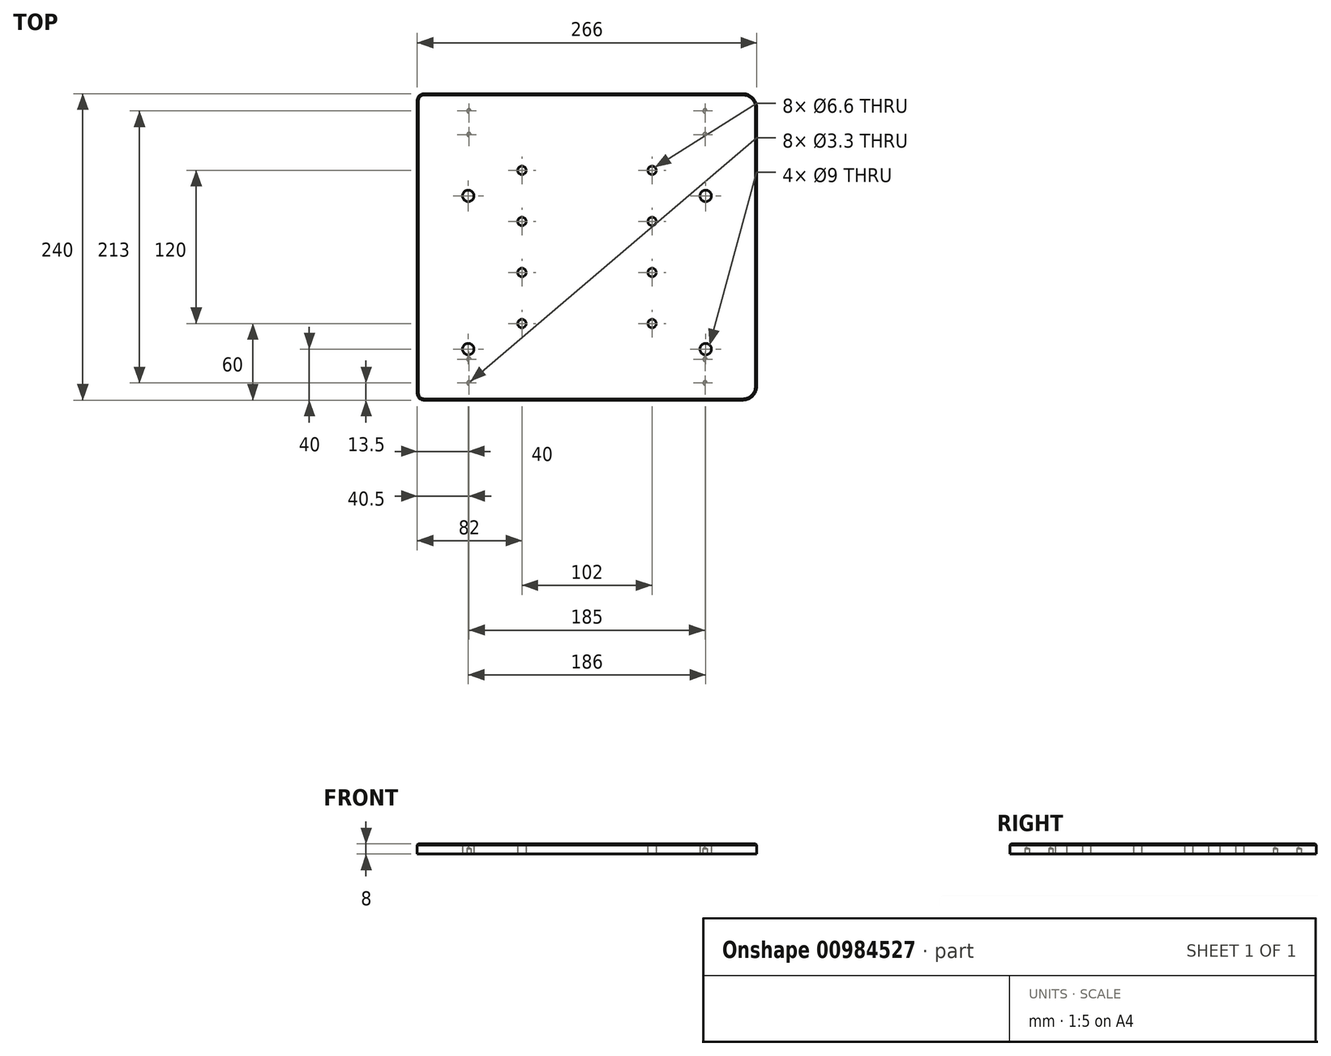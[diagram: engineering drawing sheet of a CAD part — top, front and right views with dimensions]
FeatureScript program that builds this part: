
annotation { "Feature Type Name" : "Feature", "Feature Type Description" : "" }
export const myFeature = defineFeature(function(context is Context, id is Id, definition is map)
    precondition{}
    {
        {
            var Q0;
            Q0=qCreatedBy(makeId("Top.planeOp"),FACE);
            var sketch = newSketch(context, id + "F0", { "sketchPlane" : qUnion([Q0])});
            skLineSegment(sketch, "E0.bottom", {"start": v(122.23, -120) * mm, "end": v(-127.75, -120) * mm});
            skLineSegment(sketch, "E0.top", {"start": v(122.23, 120) * mm, "end": v(-127.75, 120) * mm});
            skLineSegment(sketch, "E0.left", {"start": v(133, -109.23) * mm, "end": v(133, 109.23) * mm});
            skLineSegment(sketch, "E0.right", {"start": v(-133, -114.75) * mm, "end": v(-133, 114.75) * mm});
            skPoint(sketch, "E0.middle", {"position": v(0, 0) * mm});
            skPoint(sketch, "E1.visualSharp", {"position": v(133, 120) * mm});
            skArc(sketch, "E1.filletArc", {"start": v(133, 109.23) * mm, "mid": v(129.85, 116.85) * mm, "end": v(122.23, 120) * mm});
            skPoint(sketch, "E2.visualSharp", {"position": v(133, -120) * mm});
            skArc(sketch, "E2.filletArc", {"start": v(122.23, -120) * mm, "mid": v(129.85, -116.85) * mm, "end": v(133, -109.23) * mm});
            skPoint(sketch, "E3.visualSharp", {"position": v(-133, -120) * mm});
            skArc(sketch, "E3.filletArc", {"start": v(-133, -114.75) * mm, "mid": v(-131.46, -118.46) * mm, "end": v(-127.75, -120) * mm});
            skPoint(sketch, "E4.visualSharp", {"position": v(-133, 120) * mm});
            skArc(sketch, "E4.filletArc", {"start": v(-127.75, 120) * mm, "mid": v(-131.46, 118.46) * mm, "end": v(-133, 114.75) * mm});
            skPoint(sketch, "E5", {"position": v(-93, -80) * mm});
            skPoint(sketch, "E6", {"position": v(-93, 40) * mm});
            skPoint(sketch, "E7", {"position": v(93, 40) * mm});
            skPoint(sketch, "E8", {"position": v(93, -80) * mm});
            skPoint(sketch, "E9", {"position": v(-51, -60) * mm});
            skPoint(sketch, "E10", {"position": v(-51, -20) * mm});
            skPoint(sketch, "E11", {"position": v(-51, 20) * mm});
            skPoint(sketch, "E12", {"position": v(-51, 60) * mm});
            skPoint(sketch, "E13", {"position": v(51, 60) * mm});
            skPoint(sketch, "E14", {"position": v(51, 20) * mm});
            skPoint(sketch, "E15", {"position": v(51, -60) * mm});
            skPoint(sketch, "E16", {"position": v(51, -20) * mm});
            skPoint(sketch, "E17", {"position": v(-92.5, -106.5) * mm});
            skPoint(sketch, "E18", {"position": v(-92.5, -88) * mm});
            skPoint(sketch, "E19", {"position": v(-92.5, 106.5) * mm});
            skPoint(sketch, "E20", {"position": v(-92.5, 88) * mm});
            skPoint(sketch, "E21.MirrorP", {"position": v(92.5, -106.5) * mm});
            skPoint(sketch, "E22.MirrorP", {"position": v(92.5, -88) * mm});
            skPoint(sketch, "E23.MirrorP", {"position": v(92.5, 88) * mm});
            skPoint(sketch, "E24.MirrorP", {"position": v(92.5, 106.5) * mm});
            skSolve(sketch);
        }
        {
            var Q0;
            Q0=makeQuery(id+"F0.imprint","IMPRINT",FACE,{"disambiguationData":[TD([[makeQuery(id+"F0.imprint","IMPRINT",EDGE,{"derivedFrom":sQuery(id+"F0.wireOp",EDGE,"E0.bottom")}),-1.0]])]});
            extrude(context, id + "F1", {"entities" : qUnion([Q0]), "depth" : 8 * mm, "offsetDistance" : 25 * mm});
        }
        {
            var Q0;
            Q0=makeQuery(id+"F1.opExtrude","CAP_FACE",FACE,{"disambiguationData":[OSD([sQuery(id+"F0.wireOp",EDGE,"E0.bottom"),sQuery(id+"F0.wireOp",EDGE,"E0.top"),sQuery(id+"F0.wireOp",EDGE,"E0.left"),sQuery(id+"F0.wireOp",EDGE,"E0.right"),sQuery(id+"F0.wireOp",EDGE,"E1.filletArc"),sQuery(id+"F0.wireOp",EDGE,"E2.filletArc"),sQuery(id+"F0.wireOp",EDGE,"E3.filletArc"),sQuery(id+"F0.wireOp",EDGE,"E4.filletArc")])],"isStart":false});
            chamfer(context, id + "F2", {"entities" : qUnion([Q0]), "width" : 1 * mm, "tangentPropagation" : true});
        }
        {
            var Q0;
            Q0=sQuery(id+"F0.wireOp",VERTEX,"E9");
            var Q1;
            Q1=sQuery(id+"F0.wireOp",VERTEX,"E10");
            var Q2;
            Q2=sQuery(id+"F0.wireOp",VERTEX,"E11");
            var Q3;
            Q3=sQuery(id+"F0.wireOp",VERTEX,"E12");
            var Q4;
            Q4=sQuery(id+"F0.wireOp",VERTEX,"E13");
            var Q5;
            Q5=sQuery(id+"F0.wireOp",VERTEX,"E14");
            var Q6;
            Q6=sQuery(id+"F0.wireOp",VERTEX,"E16");
            var Q7;
            Q7=sQuery(id+"F0.wireOp",VERTEX,"E15");
            var Q8;
            Q8=makeQuery(id+"F1.opExtrude","SWEPT_BODY",BODY,{"disambiguationData":[OSD([sQuery(id+"F0.wireOp",EDGE,"E0.bottom"),sQuery(id+"F0.wireOp",EDGE,"E0.top"),sQuery(id+"F0.wireOp",EDGE,"E0.left"),sQuery(id+"F0.wireOp",EDGE,"E0.right"),sQuery(id+"F0.wireOp",EDGE,"E1.filletArc"),sQuery(id+"F0.wireOp",EDGE,"E2.filletArc"),sQuery(id+"F0.wireOp",EDGE,"E3.filletArc"),sQuery(id+"F0.wireOp",EDGE,"E4.filletArc")])]});
            hole(context, id + "F3", {"style" : HoleStyle.SIMPLE, "endStyle" : HoleEndStyle.THROUGH, "oppositeDirection" : true, "standardTappedOrClearance" : lookupTablePath({ "fit" : "Normal", "standard" : "ISO", "size" : "M6", "type" : "Clearance" }), "standardBlindInLast" : lookupTablePath({ "fit" : "Normal", "standard" : "ISO", "engagement" : "75%", "pitch" : "1 mm", "size" : "M6", "type" : "Clearance & tapped" }), "holeDiameter" : 6.6 * mm, "majorDiameter" : 5 * mm, "isTappedThrough" : true, "tappedDepth" : 12 * mm, "tapClearance" : 3, "locations" : qUnion([Q0, Q1, Q2, Q3, Q4, Q5, Q6, Q7]), "scope" : qUnion([Q8])});
        }
        {
            var Q0;
            Q0=sQuery(id+"F0.wireOp",VERTEX,"E5");
            var Q1;
            Q1=sQuery(id+"F0.wireOp",VERTEX,"E6");
            var Q2;
            Q2=sQuery(id+"F0.wireOp",VERTEX,"E7");
            var Q3;
            Q3=sQuery(id+"F0.wireOp",VERTEX,"E8");
            var Q4;
            Q4=makeQuery(id+"F1.opExtrude","SWEPT_BODY",BODY,{"disambiguationData":[OSD([sQuery(id+"F0.wireOp",EDGE,"E0.bottom"),sQuery(id+"F0.wireOp",EDGE,"E0.top"),sQuery(id+"F0.wireOp",EDGE,"E0.left"),sQuery(id+"F0.wireOp",EDGE,"E0.right"),sQuery(id+"F0.wireOp",EDGE,"E1.filletArc"),sQuery(id+"F0.wireOp",EDGE,"E2.filletArc"),sQuery(id+"F0.wireOp",EDGE,"E3.filletArc"),sQuery(id+"F0.wireOp",EDGE,"E4.filletArc")])]});
            hole(context, id + "F4", {"style" : HoleStyle.SIMPLE, "endStyle" : HoleEndStyle.THROUGH, "oppositeDirection" : true, "standardTappedOrClearance" : lookupTablePath({ "fit" : "Normal", "standard" : "ISO", "size" : "M8", "type" : "Clearance" }), "standardBlindInLast" : lookupTablePath({ "fit" : "Normal", "standard" : "ISO", "engagement" : "75%", "pitch" : "1.25 mm", "size" : "M8", "type" : "Clearance & tapped" }), "holeDiameter" : 9 * mm, "majorDiameter" : 5 * mm, "isTappedThrough" : true, "tappedDepth" : 12 * mm, "tapClearance" : 3, "locations" : qUnion([Q0, Q1, Q2, Q3]), "scope" : qUnion([Q4])});
        }
        {
            var Q0;
            Q0=sQuery(id+"F0.wireOp",VERTEX,"E18");
            var Q1;
            Q1=sQuery(id+"F0.wireOp",VERTEX,"E17");
            var Q2;
            Q2=sQuery(id+"F0.wireOp",VERTEX,"E22.MirrorP");
            var Q3;
            Q3=sQuery(id+"F0.wireOp",VERTEX,"E21.MirrorP");
            var Q4;
            Q4=sQuery(id+"F0.wireOp",VERTEX,"E23.MirrorP");
            var Q5;
            Q5=sQuery(id+"F0.wireOp",VERTEX,"E24.MirrorP");
            var Q6;
            Q6=sQuery(id+"F0.wireOp",VERTEX,"E20");
            var Q7;
            Q7=sQuery(id+"F0.wireOp",VERTEX,"E19");
            var Q8;
            Q8=makeQuery(id+"F1.opExtrude","SWEPT_BODY",BODY,{"disambiguationData":[OSD([sQuery(id+"F0.wireOp",EDGE,"E0.bottom"),sQuery(id+"F0.wireOp",EDGE,"E0.top"),sQuery(id+"F0.wireOp",EDGE,"E0.left"),sQuery(id+"F0.wireOp",EDGE,"E0.right"),sQuery(id+"F0.wireOp",EDGE,"E1.filletArc"),sQuery(id+"F0.wireOp",EDGE,"E2.filletArc"),sQuery(id+"F0.wireOp",EDGE,"E3.filletArc"),sQuery(id+"F0.wireOp",EDGE,"E4.filletArc")])]});
            hole(context, id + "F5", {"style" : HoleStyle.SIMPLE, "endStyle" : HoleEndStyle.BLIND, "oppositeDirection" : true, "standardTappedOrClearance" : lookupTablePath({ "standard" : "ISO", "engagement" : "75%", "pitch" : "0.7 mm", "size" : "M4", "type" : "Tapped" }), "standardBlindInLast" : lookupTablePath({ "standard" : "ISO", "fit" : "Normal", "engagement" : "75%", "pitch" : "0.7 mm", "size" : "M4", "type" : "Clearance & tapped" }), "holeDiameter" : 3.3 * mm, "majorDiameter" : 4 * mm, "showTappedDepth" : true, "holeDepth" : 4.35 * mm, "isTappedThrough" : true, "tappedDepth" : 2.25 * mm, "tapClearance" : 3, "locations" : qUnion([Q0, Q1, Q2, Q3, Q4, Q5, Q6, Q7]), "scope" : qUnion([Q8])});
        }
    });
